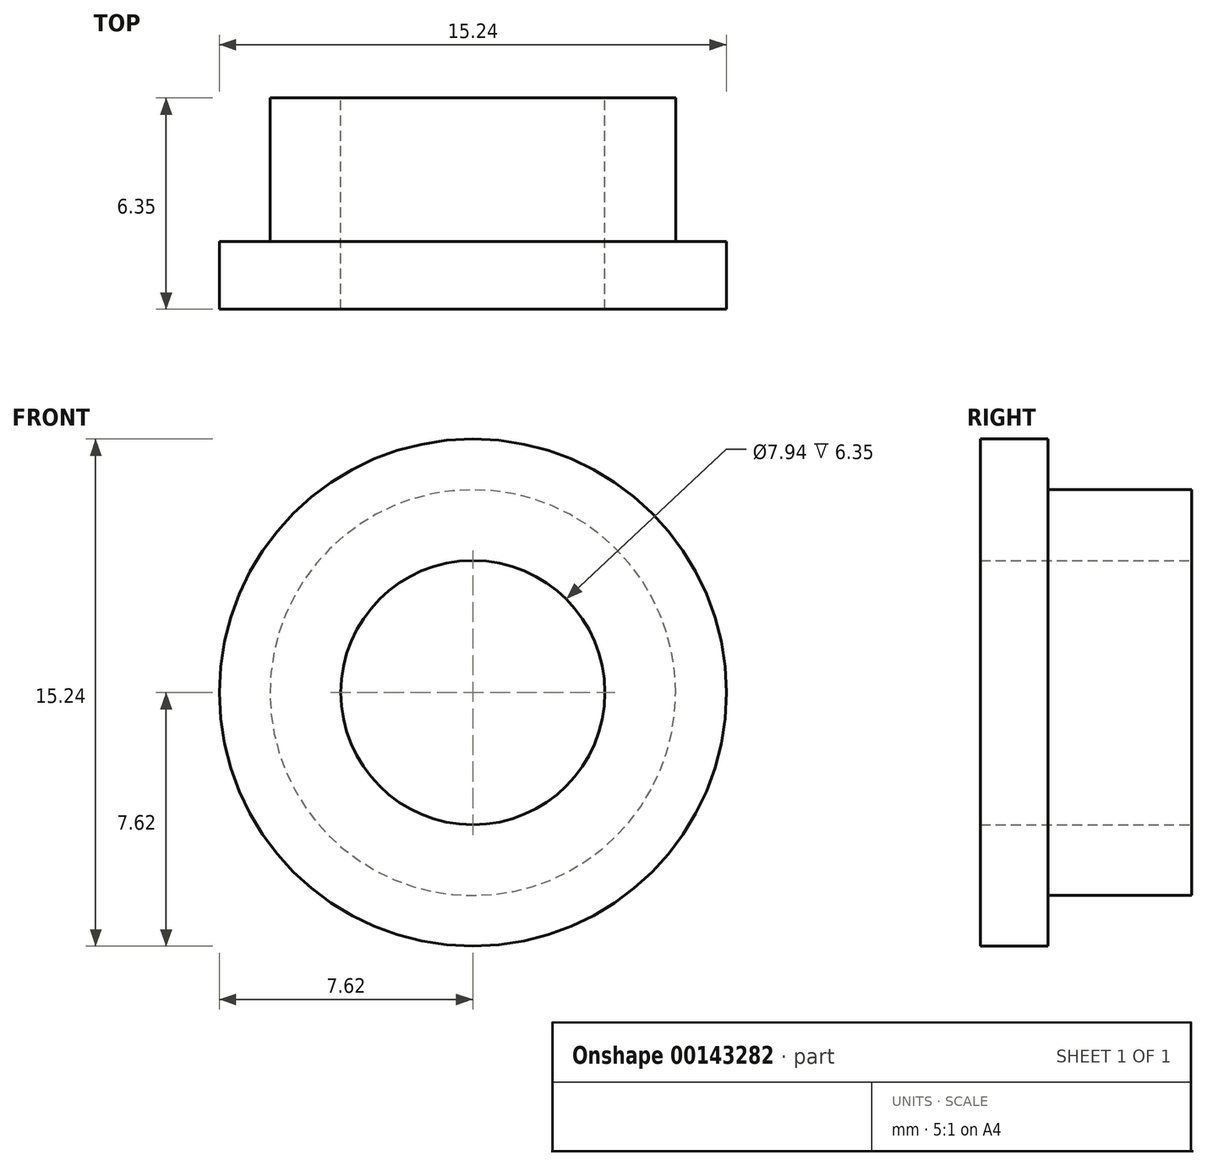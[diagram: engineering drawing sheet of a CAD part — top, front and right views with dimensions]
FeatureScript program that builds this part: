
annotation { "Feature Type Name" : "Feature", "Feature Type Description" : "" }
export const myFeature = defineFeature(function(context is Context, id is Id, definition is map)
    precondition{}
    {
        {
            var Q0;
            Q0=qCreatedBy(makeId("Front.planeOp"),FACE);
            var sketch = newSketch(context, id + "F0", { "sketchPlane" : qUnion([Q0])});
            skCircle(sketch, "E0", {"center": v(0, 0) * mm, "radius": 6.1 * mm});
            skCircle(sketch, "E1", {"center": v(0, 0) * mm, "radius": 3.97 * mm});
            skSolve(sketch);
        }
        {
            var Q0;
            Q0 = qSketchRegion(id + "F0", true);
            extrude(context, id + "F1", {"entities" : qUnion([Q0]), "depth" : 6.35 * mm});
        }
        {
            var Q0;
            Q0=makeQuery(id+"F1.opExtrude","CAP_FACE",FACE,{"disambiguationData":[OSD([sQuery(id+"F0.wireOp",EDGE,"E0"),sQuery(id+"F0.wireOp",EDGE,"E1")])],"isStart":false});
            var sketch = newSketch(context, id + "F2", { "sketchPlane" : qUnion([Q0])});
            skCircle(sketch, "E2", {"center": v(0, 0) * mm, "radius": 7.62 * mm});
            skCircle(sketch, "E3", {"center": v(0, 0) * mm, "radius": 3.97 * mm});
            skSolve(sketch);
        }
        {
            var Q0;
            Q0 = qSketchRegion(id + "F2", true);
            extrude(context, id + "F3", {"entities" : qUnion([Q0]), "operationType" : NewBodyOperationType.ADD, "oppositeDirection" : true, "depth" : 2.03 * mm});
        }
    });
